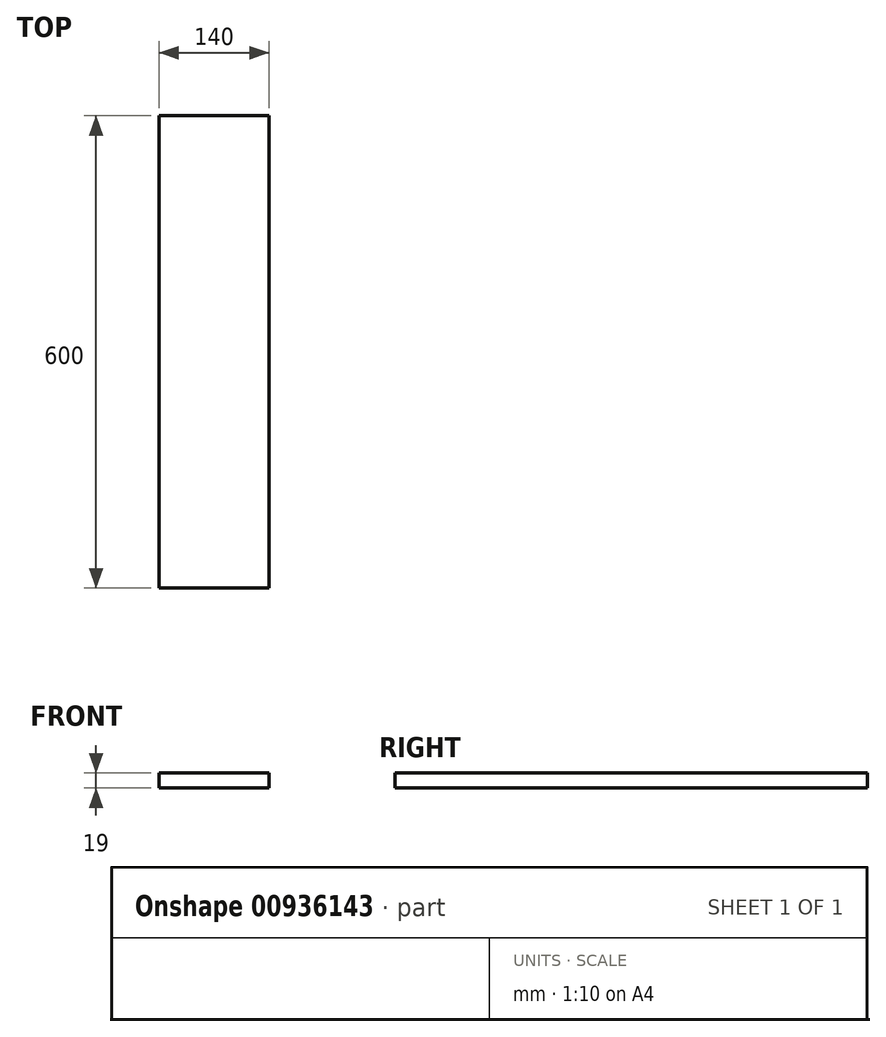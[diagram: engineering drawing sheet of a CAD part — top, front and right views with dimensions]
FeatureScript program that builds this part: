
annotation { "Feature Type Name" : "Feature", "Feature Type Description" : "" }
export const myFeature = defineFeature(function(context is Context, id is Id, definition is map)
    precondition{}
    {
        {
            var Q0;
            Q0=qCreatedBy(makeId("Front.planeOp"),FACE);
            var sketch = newSketch(context, id + "F0", { "sketchPlane" : qUnion([Q0])});
            skLineSegment(sketch, "E0.bottom", {"start": v(0, 0) * mm, "end": v(140, 0) * mm});
            skLineSegment(sketch, "E0.top", {"start": v(0, 19) * mm, "end": v(140, 19) * mm});
            skLineSegment(sketch, "E0.left", {"start": v(0, 0) * mm, "end": v(0, 19) * mm});
            skLineSegment(sketch, "E0.right", {"start": v(140, 0) * mm, "end": v(140, 19) * mm});
            skSolve(sketch);
        }
        {
            var Q0;
            Q0=makeQuery(id+"F0.imprint","IMPRINT",FACE,{"disambiguationData":[TD([[makeQuery(id+"F0.imprint","IMPRINT",EDGE,{"derivedFrom":sQuery(id+"F0.wireOp",EDGE,"E0.bottom")}),1.0]])]});
            extrude(context, id + "F1", {"entities" : qUnion([Q0]), "depth" : 600 * mm, "offsetDistance" : 25 * mm});
        }
    });
